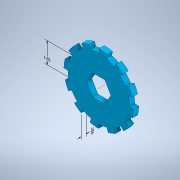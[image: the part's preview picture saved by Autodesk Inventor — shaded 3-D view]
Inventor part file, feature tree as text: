
AUTODESK INVENTOR PART (.ipt)
format: ipt  version: 2022.2 (Build 262287000, 287)  size: 703,488 bytes
history: native  units: in
note: dims shown in document units (in); Inventor stores cm internally (conversion verified against a paired STEP export)
features: sketch x4, other x3, extrude x3, pattern_circular x1, emboss x1
ambient origin geometry x8: Origin, YZ Plane, XZ Plane, XY Plane, X Axis, Y Axis, Z Axis, Center Point
bodies: Solid1 (feature_tree)
feature tree (12):
  other  "Annotations"
  extrude  "Extrusion1"  Depth=0.25in TaperAngle=0.0deg
  extrude  "Extrusion11"  TaperAngle=0.0deg  [1 undecoded]
  extrude  "Extrusion19"  Depth=0.0034in
  pattern_circular  "Circular Pattern11"  [2 undecoded]
  emboss  "Emboss1"
  sketch  "Sketch1"  dims[d0=2.985in d1=0.25in d2=0.0in]
  sketch  "Sketch10"  dims[d55=1.015in d56=0.0in d57=0.0in]
  sketch  "Sketch17"  dims[d123=0.1963in d124=0.0034in]
  sketch  "Sketch35"  dims[d125=0.0962in d126=0.25in d127=0.0in d128=4.7244in d129=360.0deg d131=2.985in d132=3.3777in d212=2.0in d213=0.1in d214=0.0in d136=0.25in d209=0.2158in d210=0.2107in d211=1.015in]
  other  "Linear Dimension 2"
  other  "Linear Dimension 3"
note: 3 required parameter values undecoded (feature->parameter linkage not recoverable at this tier; creation-order binding heuristic only, values carry confidence <= 0.55)
